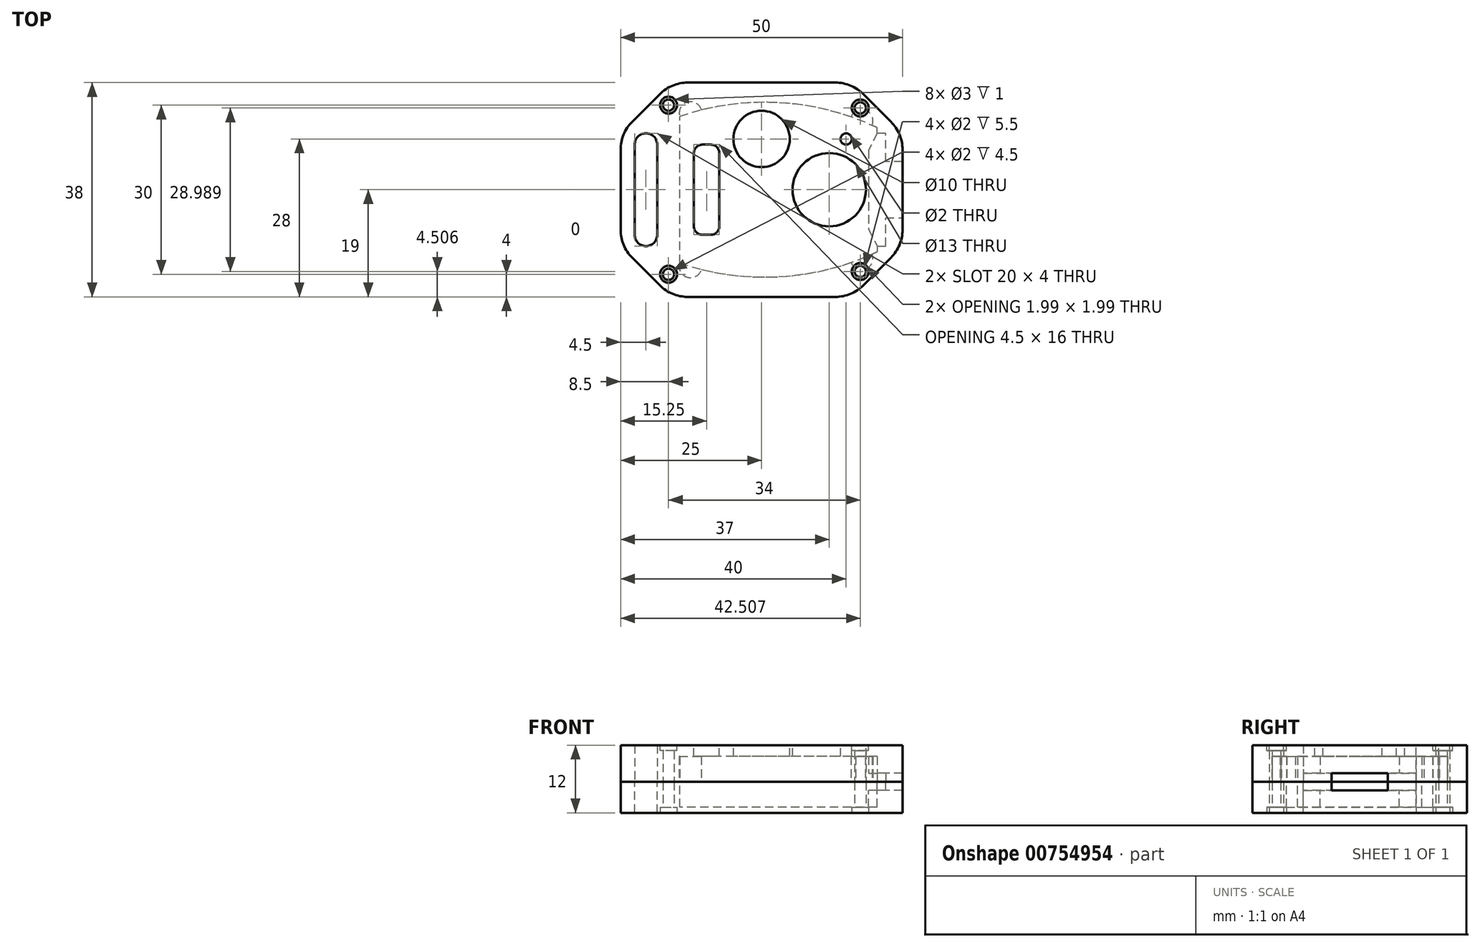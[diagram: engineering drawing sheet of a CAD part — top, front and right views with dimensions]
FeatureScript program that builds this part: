
annotation { "Feature Type Name" : "Feature", "Feature Type Description" : "" }
export const myFeature = defineFeature(function(context is Context, id is Id, definition is map)
    precondition{}
    {
        {
            var Q0;
            Q0=qCreatedBy(makeId("Top.planeOp"),FACE);
            var sketch = newSketch(context, id + "F0", { "sketchPlane" : qUnion([Q0])});
            skLineSegment(sketch, "E0.bottom", {"start": v(25, 19) * mm, "end": v(-25, 19) * mm});
            skLineSegment(sketch, "E0.top", {"start": v(25, -19) * mm, "end": v(-25, -19) * mm});
            skLineSegment(sketch, "E0.left", {"start": v(25, 19) * mm, "end": v(25, -19) * mm});
            skLineSegment(sketch, "E0.right", {"start": v(-25, 19) * mm, "end": v(-25, -19) * mm});
            skPoint(sketch, "E0.middle", {"position": v(0, 0) * mm});
            skLineSegment(sketch, "E1", {"start": v(25, 5) * mm, "end": v(22, 5) * mm});
            skLineSegment(sketch, "E2", {"start": v(22, 5) * mm, "end": v(22, 10) * mm});
            skLineSegment(sketch, "E3", {"start": v(22, 10) * mm, "end": v(20.5, 10) * mm});
            skLineSegment(sketch, "E4", {"start": v(20.5, 10) * mm, "end": v(19, 7) * mm});
            skLineSegment(sketch, "E5", {"start": v(19, 7) * mm, "end": v(19, -7) * mm});
            skLineSegment(sketch, "E6", {"start": v(19, -7) * mm, "end": v(20.5, -10) * mm});
            skLineSegment(sketch, "E7", {"start": v(20.5, -10) * mm, "end": v(22, -10) * mm});
            skLineSegment(sketch, "E8", {"start": v(22, -10) * mm, "end": v(22, -5) * mm});
            skLineSegment(sketch, "E9", {"start": v(22, -5) * mm, "end": v(25, -5) * mm});
            skSolve(sketch);
        }
        {
            var Q0;
            {var subQ1=sQuery(id+"F0.wireOp",EDGE,"E0.bottom");Q0=makeQuery(id+"F0.imprint","IMPRINT",FACE,{"disambiguationData":[TD([[makeQuery(id+"F0.imprint","IMPRINT",EDGE,{"derivedFrom":subQ1}),1.0]])]});}
            var Q1;
            {var subQ0=sQuery(id+"F0.wireOp",EDGE,"E1");Q1=makeQuery(id+"F0.imprint","IMPRINT",FACE,{"disambiguationData":[TD([[makeQuery(id+"F0.imprint","IMPRINT",EDGE,{"derivedFrom":subQ0}),1.0]])]});}
            extrude(context, id + "F1", {"entities" : qUnion([Q0, Q1]), "oppositeDirection" : true, "depth" : 5.5 * mm, "offsetDistance" : 25 * mm});
        }
        {
            var Q0;
            {var subQ0=sQuery(id+"F0.wireOp",EDGE,"E1");Q0=makeQuery(id+"F0.imprint","IMPRINT",FACE,{"disambiguationData":[TD([[makeQuery(id+"F0.imprint","IMPRINT",EDGE,{"derivedFrom":subQ0}),1.0]])]});}
            extrude(context, id + "F2", {"entities" : qUnion([Q0]), "operationType" : NewBodyOperationType.REMOVE, "oppositeDirection" : true, "depth" : 1.5 * mm, "offsetDistance" : 25 * mm});
        }
        {
            var Q0;
            {var subQ1=sQuery(id+"F0.wireOp",EDGE,"E0.bottom");Q0=makeQuery(id+"F0.imprint","IMPRINT",FACE,{"disambiguationData":[TD([[makeQuery(id+"F0.imprint","IMPRINT",EDGE,{"derivedFrom":subQ1}),1.0]])]});}
            var sketch = newSketch(context, id + "F3", { "sketchPlane" : qUnion([Q0])});
            skLineSegment(sketch, "E10.0", {"start": v(20.5, 10) * mm, "end": v(19, 7) * mm});
            skLineSegment(sketch, "E11.0", {"start": v(19, 7) * mm, "end": v(19, -7) * mm});
            skLineSegment(sketch, "E12.0", {"start": v(19, -7) * mm, "end": v(20.5, -10) * mm});
            skLineSegment(sketch, "E13", {"start": v(-14.5, 0) * mm, "end": v(-14.5, 13) * mm});
            skLineSegment(sketch, "E14", {"start": v(-14.5, 0) * mm, "end": v(-14.5, -13) * mm});
            skPoint(sketch, "E15.end.orphan", {"position": v(0.5, 15.5) * mm});
            skPoint(sketch, "E16.end.orphan", {"position": v(0.5, -15.5) * mm});
            skPoint(sketch, "E16.start.orphan", {"position": v(-4.79, 0) * mm});
            skLineSegment(sketch, "E17", {"start": v(20.5, 10) * mm, "end": v(20.5, 11) * mm});
            skLineSegment(sketch, "E18", {"start": v(20.5, -10) * mm, "end": v(20.5, -11) * mm});
            skArc(sketch, "E19", {"start": v(20.5, 11) * mm, "mid": v(3.2, 15.42) * mm, "end": v(-14.5, 13) * mm});
            skArc(sketch, "E20", {"start": v(-14.5, -13) * mm, "mid": v(3.2, -15.42) * mm, "end": v(20.5, -11) * mm});
            skSolve(sketch);
        }
        {
            var Q0;
            Q0=makeQuery(id+"F3.imprint","IMPRINT",FACE,{"disambiguationData":[TD([[makeQuery(id+"F3.imprint","IMPRINT",EDGE,{"derivedFrom":sQuery(id+"F3.wireOp",EDGE,"E10.0")}),-1.0]])]});
            extrude(context, id + "F4", {"entities" : qUnion([Q0]), "operationType" : NewBodyOperationType.REMOVE, "oppositeDirection" : true, "depth" : 4.5 * mm, "offsetDistance" : 25 * mm});
        }
        {
            var Q0;
            Q0=makeQuery(id+"F1.opExtrude","CAP_FACE",FACE,{"disambiguationData":[OSD([sQuery(id+"F0.wireOp",EDGE,"E0.bottom"),sQuery(id+"F0.wireOp",EDGE,"E0.top"),sQuery(id+"F0.wireOp",EDGE,"E0.left"),sQuery(id+"F0.wireOp",EDGE,"E0.right")])],"isStart":true});
            var sketch = newSketch(context, id + "F5", { "sketchPlane" : qUnion([Q0])});
            skLineSegment(sketch, "E21.bottom", {"start": v(-18.5, 10) * mm, "end": v(-22.5, 10) * mm});
            skLineSegment(sketch, "E21.top", {"start": v(-18.5, -10) * mm, "end": v(-22.5, -10) * mm});
            skLineSegment(sketch, "E21.left", {"start": v(-18.5, 10) * mm, "end": v(-18.5, -10) * mm});
            skLineSegment(sketch, "E21.right", {"start": v(-22.5, 10) * mm, "end": v(-22.5, -10) * mm});
            skPoint(sketch, "E21.middle", {"position": v(-20.5, 0) * mm});
            skSolve(sketch);
        }
        {
            var Q0;
            Q0=makeQuery(id+"F5.imprint","IMPRINT",FACE,{"disambiguationData":[TD([[makeQuery(id+"F5.imprint","IMPRINT",EDGE,{"derivedFrom":sQuery(id+"F5.wireOp",EDGE,"E21.bottom")}),1.0]])]});
            extrude(context, id + "F6", {"entities" : qUnion([Q0]), "operationType" : NewBodyOperationType.REMOVE, "oppositeDirection" : true, "depth" : 25 * mm, "offsetDistance" : 25 * mm});
        }
        {
            var Q0;
            {var subQ1=sQuery(id+"F0.wireOp",EDGE,"E0.bottom");Q0=makeQuery(id+"F0.imprint","IMPRINT",FACE,{"disambiguationData":[TD([[makeQuery(id+"F0.imprint","IMPRINT",EDGE,{"derivedFrom":subQ1}),1.0]])]});}
            var Q1;
            {var subQ0=sQuery(id+"F0.wireOp",EDGE,"E1");Q1=makeQuery(id+"F0.imprint","IMPRINT",FACE,{"disambiguationData":[TD([[makeQuery(id+"F0.imprint","IMPRINT",EDGE,{"derivedFrom":subQ0}),1.0]])]});}
            extrude(context, id + "F7", {"entities" : qUnion([Q0, Q1]), "depth" : 6.5 * mm, "offsetDistance" : 25 * mm});
        }
        {
            var Q0;
            {var subQ0=sQuery(id+"F0.wireOp",EDGE,"E1");Q0=makeQuery(id+"F0.imprint","IMPRINT",FACE,{"disambiguationData":[TD([[makeQuery(id+"F0.imprint","IMPRINT",EDGE,{"derivedFrom":subQ0}),1.0]])]});}
            extrude(context, id + "F8", {"entities" : qUnion([Q0]), "operationType" : NewBodyOperationType.REMOVE, "depth" : 1.5 * mm, "offsetDistance" : 25 * mm});
        }
        {
            var Q0;
            Q0=makeQuery(id+"F3.imprint","IMPRINT",FACE,{"disambiguationData":[TD([[makeQuery(id+"F3.imprint","IMPRINT",EDGE,{"derivedFrom":sQuery(id+"F3.wireOp",EDGE,"E10.0")}),-1.0]])]});
            extrude(context, id + "F9", {"entities" : qUnion([Q0]), "operationType" : NewBodyOperationType.REMOVE, "depth" : 4.5 * mm, "offsetDistance" : 25 * mm});
        }
        {
            var Q0;
            Q0=makeQuery(id+"F5.imprint","IMPRINT",FACE,{"disambiguationData":[TD([[makeQuery(id+"F5.imprint","IMPRINT",EDGE,{"derivedFrom":sQuery(id+"F5.wireOp",EDGE,"E21.bottom")}),1.0]])]});
            extrude(context, id + "F10", {"entities" : qUnion([Q0]), "operationType" : NewBodyOperationType.REMOVE, "depth" : 25 * mm, "offsetDistance" : 25 * mm});
        }
        {
            var Q0;
            Q0=makeQuery(id+"F7.opExtrude","CAP_FACE",FACE,{"disambiguationData":[OSD([sQuery(id+"F0.wireOp",EDGE,"E0.bottom"),sQuery(id+"F0.wireOp",EDGE,"E0.top"),sQuery(id+"F0.wireOp",EDGE,"E0.left"),sQuery(id+"F0.wireOp",EDGE,"E0.right")])],"isStart":false});
            var sketch = newSketch(context, id + "F11", { "sketchPlane" : qUnion([Q0])});
            skCircle(sketch, "E22", {"center": v(12, 0) * mm, "radius": 6.5 * mm});
            skCircle(sketch, "E23", {"center": v(0, 9) * mm, "radius": 5 * mm});
            skLineSegment(sketch, "E24.bottom", {"start": v(-9, 8) * mm, "end": v(-10.5, 8) * mm});
            skLineSegment(sketch, "E24.top", {"start": v(-9, -8) * mm, "end": v(-10.5, -8) * mm});
            skLineSegment(sketch, "E24.left", {"start": v(-7.5, 6.5) * mm, "end": v(-7.5, -6.5) * mm});
            skLineSegment(sketch, "E24.right", {"start": v(-12, 6.5) * mm, "end": v(-12, -6.5) * mm});
            skPoint(sketch, "E24.middle", {"position": v(-9.75, 0) * mm});
            skPoint(sketch, "E25.visualSharp", {"position": v(-12, 8) * mm});
            skArc(sketch, "E25.filletArc", {"start": v(-10.5, 8) * mm, "mid": v(-11.56, 7.56) * mm, "end": v(-12, 6.5) * mm});
            skPoint(sketch, "E26.visualSharp", {"position": v(-7.5, 8) * mm});
            skArc(sketch, "E26.filletArc", {"start": v(-7.5, 6.5) * mm, "mid": v(-7.94, 7.56) * mm, "end": v(-9, 8) * mm});
            skPoint(sketch, "E27.visualSharp", {"position": v(-7.5, -8) * mm});
            skArc(sketch, "E27.filletArc", {"start": v(-9, -8) * mm, "mid": v(-7.94, -7.56) * mm, "end": v(-7.5, -6.5) * mm});
            skPoint(sketch, "E28.visualSharp", {"position": v(-12, -8) * mm});
            skArc(sketch, "E28.filletArc", {"start": v(-12, -6.5) * mm, "mid": v(-11.56, -7.56) * mm, "end": v(-10.5, -8) * mm});
            skCircle(sketch, "E29", {"center": v(15, 9) * mm, "radius": 1 * mm});
            skSolve(sketch);
        }
        {
            var Q0;
            Q0=makeQuery(id+"F11.imprint","IMPRINT",FACE,{"disambiguationData":[TD([[makeQuery(id+"F11.imprint","IMPRINT",EDGE,{"derivedFrom":sQuery(id+"F11.wireOp",EDGE,"E23")}),1.0]])]});
            var Q1;
            Q1=makeQuery(id+"F11.imprint","IMPRINT",FACE,{"disambiguationData":[TD([[makeQuery(id+"F11.imprint","IMPRINT",EDGE,{"derivedFrom":sQuery(id+"F11.wireOp",EDGE,"E24.bottom")}),1.0]])]});
            var Q2;
            Q2=makeQuery(id+"F11.imprint","IMPRINT",FACE,{"disambiguationData":[TD([[makeQuery(id+"F11.imprint","IMPRINT",EDGE,{"derivedFrom":sQuery(id+"F11.wireOp",EDGE,"E22")}),1.0]])]});
            var Q3;
            Q3=makeQuery(id+"F11.imprint","IMPRINT",FACE,{"disambiguationData":[TD([[makeQuery(id+"F11.imprint","IMPRINT",EDGE,{"derivedFrom":sQuery(id+"F11.wireOp",EDGE,"E29")}),1.0]])]});
            extrude(context, id + "F12", {"entities" : qUnion([Q0, Q1, Q2, Q3]), "operationType" : NewBodyOperationType.REMOVE, "oppositeDirection" : true, "depth" : 4 * mm, "offsetDistance" : 25 * mm});
        }
        {
            var Q0;
            Q0=makeQuery(id+"F3.imprint","IMPRINT",FACE,{"disambiguationData":[TD([[makeQuery(id+"F3.imprint","IMPRINT",EDGE,{"derivedFrom":sQuery(id+"F3.wireOp",EDGE,"E13")}),1.0]])]});
            var sketch = newSketch(context, id + "F13", { "sketchPlane" : qUnion([Q0])});
            skArc(sketch, "E30.0", {"start": v(-14.5, -13) * mm, "mid": v(3.2, -15.42) * mm, "end": v(20.5, -11) * mm});
            skArc(sketch, "E31.0", {"start": v(20.5, 11) * mm, "mid": v(3.2, 15.42) * mm, "end": v(-14.5, 13) * mm});
            skArc(sketch, "E32", {"start": v(-14.5, -13) * mm, "mid": v(-13.16, -15.52) * mm, "end": v(-10.66, -14.13) * mm});
            skArc(sketch, "E33", {"start": v(15.88, -12.9) * mm, "mid": v(18.5, -14.06) * mm, "end": v(19.6, -11.42) * mm});
            skArc(sketch, "E34", {"start": v(-10.66, 14.13) * mm, "mid": v(-13.16, 15.52) * mm, "end": v(-14.5, 13) * mm});
            skArc(sketch, "E35", {"start": v(19.6, 11.42) * mm, "mid": v(18.5, 14.06) * mm, "end": v(15.88, 12.9) * mm});
            skLineSegment(sketch, "E36", {"start": v(-14.5, -13) * mm, "end": v(-10.66, -14.13) * mm});
            skLineSegment(sketch, "E37", {"start": v(15.88, -12.9) * mm, "end": v(19.6, -11.42) * mm});
            skLineSegment(sketch, "E38", {"start": v(19.6, 11.42) * mm, "end": v(15.88, 12.9) * mm});
            skLineSegment(sketch, "E39", {"start": v(-10.66, 14.13) * mm, "end": v(-14.5, 13) * mm});
            skSolve(sketch);
        }
        {
            var Q0;
            Q0 = qSketchRegion(id + "F13", true);
            extrude(context, id + "F14", {"entities" : qUnion([Q0]), "operationType" : NewBodyOperationType.REMOVE, "depth" : 4.5 * mm, "offsetDistance" : 25 * mm});
        }
        {
            var Q0;
            Q0=makeQuery(id+"F7.opExtrude","SWEPT_EDGE",EDGE,{"disambiguationData":[OSD([sQuery(id+"F0.wireOp",EDGE,"E0.top"),sQuery(id+"F0.wireOp",EDGE,"E0.left")])]});
            var Q1;
            Q1=makeQuery(id+"F1.opExtrude","SWEPT_EDGE",EDGE,{"disambiguationData":[OSD([sQuery(id+"F0.wireOp",EDGE,"E0.top"),sQuery(id+"F0.wireOp",EDGE,"E0.left")])]});
            var Q2;
            Q2=makeQuery(id+"F1.opExtrude","SWEPT_EDGE",EDGE,{"disambiguationData":[OSD([sQuery(id+"F0.wireOp",EDGE,"E0.bottom"),sQuery(id+"F0.wireOp",EDGE,"E0.left")])]});
            var Q3;
            Q3=makeQuery(id+"F7.opExtrude","SWEPT_EDGE",EDGE,{"disambiguationData":[OSD([sQuery(id+"F0.wireOp",EDGE,"E0.bottom"),sQuery(id+"F0.wireOp",EDGE,"E0.left")])]});
            var Q4;
            Q4=makeQuery(id+"F7.opExtrude","SWEPT_EDGE",EDGE,{"disambiguationData":[OSD([sQuery(id+"F0.wireOp",EDGE,"E0.top"),sQuery(id+"F0.wireOp",EDGE,"E0.right")])]});
            var Q5;
            Q5=makeQuery(id+"F1.opExtrude","SWEPT_EDGE",EDGE,{"disambiguationData":[OSD([sQuery(id+"F0.wireOp",EDGE,"E0.top"),sQuery(id+"F0.wireOp",EDGE,"E0.right")])]});
            var Q6;
            Q6=makeQuery(id+"F7.opExtrude","SWEPT_EDGE",EDGE,{"disambiguationData":[OSD([sQuery(id+"F0.wireOp",EDGE,"E0.bottom"),sQuery(id+"F0.wireOp",EDGE,"E0.right")])]});
            var Q7;
            Q7=makeQuery(id+"F1.opExtrude","SWEPT_EDGE",EDGE,{"disambiguationData":[OSD([sQuery(id+"F0.wireOp",EDGE,"E0.bottom"),sQuery(id+"F0.wireOp",EDGE,"E0.right")])]});
            chamfer(context, id + "F15", {"entities" : qUnion([Q0, Q1, Q2, Q3, Q4, Q5, Q6, Q7]), "width" : 9 * mm, "tangentPropagation" : true});
        }
        {
            var Q0;
            {var subQ0=sQuery(id+"F0.wireOp",EDGE,"E0.top");Q0=makeQuery(id+"F15.opChamfer","BLEND_EDGE",EDGE,{"blendedFrom":[makeQuery(id+"F7.opExtrude","SWEPT_EDGE",EDGE,{"disambiguationData":[OSD([subQ0,sQuery(id+"F0.wireOp",EDGE,"E0.left")])]}),makeQuery(id+"F7.opExtrude","SWEPT_FACE",FACE,{"disambiguationData":[OSD([subQ0])]})],"blendedInto":[makeQuery(id+"F7.opExtrude","SWEPT_FACE",FACE,{"disambiguationData":[OSD([subQ0])]})]});}
            var Q1;
            {var subQ0=sQuery(id+"F0.wireOp",EDGE,"E0.top");Q1=makeQuery(id+"F15.opChamfer","BLEND_EDGE",EDGE,{"blendedFrom":[makeQuery(id+"F1.opExtrude","SWEPT_EDGE",EDGE,{"disambiguationData":[OSD([subQ0,sQuery(id+"F0.wireOp",EDGE,"E0.left")])]}),makeQuery(id+"F1.opExtrude","SWEPT_FACE",FACE,{"disambiguationData":[OSD([subQ0])]})],"blendedInto":[makeQuery(id+"F1.opExtrude","SWEPT_FACE",FACE,{"disambiguationData":[OSD([subQ0])]})]});}
            var Q2;
            {var subQ0=sQuery(id+"F0.wireOp",EDGE,"E0.left");Q2=makeQuery(id+"F15.opChamfer","BLEND_EDGE",EDGE,{"blendedFrom":[makeQuery(id+"F1.opExtrude","SWEPT_EDGE",EDGE,{"disambiguationData":[OSD([sQuery(id+"F0.wireOp",EDGE,"E0.top"),subQ0])]}),makeQuery(id+"F1.opExtrude","SWEPT_FACE",FACE,{"disambiguationData":[OSD([subQ0])]})],"blendedInto":[makeQuery(id+"F1.opExtrude","SWEPT_FACE",FACE,{"disambiguationData":[OSD([subQ0])]})]});}
            var Q3;
            {var subQ0=sQuery(id+"F0.wireOp",EDGE,"E0.left");Q3=makeQuery(id+"F15.opChamfer","BLEND_EDGE",EDGE,{"blendedFrom":[makeQuery(id+"F7.opExtrude","SWEPT_EDGE",EDGE,{"disambiguationData":[OSD([sQuery(id+"F0.wireOp",EDGE,"E0.top"),subQ0])]}),makeQuery(id+"F7.opExtrude","SWEPT_FACE",FACE,{"disambiguationData":[OSD([subQ0])]})],"blendedInto":[makeQuery(id+"F7.opExtrude","SWEPT_FACE",FACE,{"disambiguationData":[OSD([subQ0])]})]});}
            var Q4;
            {var subQ0=sQuery(id+"F0.wireOp",EDGE,"E0.left");Q4=makeQuery(id+"F15.opChamfer","BLEND_EDGE",EDGE,{"blendedFrom":[makeQuery(id+"F1.opExtrude","SWEPT_EDGE",EDGE,{"disambiguationData":[OSD([sQuery(id+"F0.wireOp",EDGE,"E0.bottom"),subQ0])]}),makeQuery(id+"F1.opExtrude","SWEPT_FACE",FACE,{"disambiguationData":[OSD([subQ0])]})],"blendedInto":[makeQuery(id+"F1.opExtrude","SWEPT_FACE",FACE,{"disambiguationData":[OSD([subQ0])]})]});}
            var Q5;
            {var subQ0=sQuery(id+"F0.wireOp",EDGE,"E0.left");Q5=makeQuery(id+"F15.opChamfer","BLEND_EDGE",EDGE,{"blendedFrom":[makeQuery(id+"F7.opExtrude","SWEPT_EDGE",EDGE,{"disambiguationData":[OSD([sQuery(id+"F0.wireOp",EDGE,"E0.bottom"),subQ0])]}),makeQuery(id+"F7.opExtrude","SWEPT_FACE",FACE,{"disambiguationData":[OSD([subQ0])]})],"blendedInto":[makeQuery(id+"F7.opExtrude","SWEPT_FACE",FACE,{"disambiguationData":[OSD([subQ0])]})]});}
            var Q6;
            {var subQ0=sQuery(id+"F0.wireOp",EDGE,"E0.bottom");Q6=makeQuery(id+"F15.opChamfer","BLEND_EDGE",EDGE,{"blendedFrom":[makeQuery(id+"F7.opExtrude","SWEPT_EDGE",EDGE,{"disambiguationData":[OSD([subQ0,sQuery(id+"F0.wireOp",EDGE,"E0.left")])]}),makeQuery(id+"F7.opExtrude","SWEPT_FACE",FACE,{"disambiguationData":[OSD([subQ0])]})],"blendedInto":[makeQuery(id+"F7.opExtrude","SWEPT_FACE",FACE,{"disambiguationData":[OSD([subQ0])]})]});}
            var Q7;
            {var subQ0=sQuery(id+"F0.wireOp",EDGE,"E0.bottom");Q7=makeQuery(id+"F15.opChamfer","BLEND_EDGE",EDGE,{"blendedFrom":[makeQuery(id+"F1.opExtrude","SWEPT_EDGE",EDGE,{"disambiguationData":[OSD([subQ0,sQuery(id+"F0.wireOp",EDGE,"E0.left")])]}),makeQuery(id+"F1.opExtrude","SWEPT_FACE",FACE,{"disambiguationData":[OSD([subQ0])]})],"blendedInto":[makeQuery(id+"F1.opExtrude","SWEPT_FACE",FACE,{"disambiguationData":[OSD([subQ0])]})]});}
            var Q8;
            {var subQ0=sQuery(id+"F0.wireOp",EDGE,"E0.top");Q8=makeQuery(id+"F15.opChamfer","BLEND_EDGE",EDGE,{"blendedFrom":[makeQuery(id+"F1.opExtrude","SWEPT_EDGE",EDGE,{"disambiguationData":[OSD([subQ0,sQuery(id+"F0.wireOp",EDGE,"E0.right")])]}),makeQuery(id+"F1.opExtrude","SWEPT_FACE",FACE,{"disambiguationData":[OSD([subQ0])]})],"blendedInto":[makeQuery(id+"F1.opExtrude","SWEPT_FACE",FACE,{"disambiguationData":[OSD([subQ0])]})]});}
            var Q9;
            {var subQ0=sQuery(id+"F0.wireOp",EDGE,"E0.top");Q9=makeQuery(id+"F15.opChamfer","BLEND_EDGE",EDGE,{"blendedFrom":[makeQuery(id+"F7.opExtrude","SWEPT_EDGE",EDGE,{"disambiguationData":[OSD([subQ0,sQuery(id+"F0.wireOp",EDGE,"E0.right")])]}),makeQuery(id+"F7.opExtrude","SWEPT_FACE",FACE,{"disambiguationData":[OSD([subQ0])]})],"blendedInto":[makeQuery(id+"F7.opExtrude","SWEPT_FACE",FACE,{"disambiguationData":[OSD([subQ0])]})]});}
            var Q10;
            {var subQ0=sQuery(id+"F0.wireOp",EDGE,"E0.right");Q10=makeQuery(id+"F15.opChamfer","BLEND_EDGE",EDGE,{"blendedFrom":[makeQuery(id+"F7.opExtrude","SWEPT_EDGE",EDGE,{"disambiguationData":[OSD([sQuery(id+"F0.wireOp",EDGE,"E0.top"),subQ0])]}),makeQuery(id+"F7.opExtrude","SWEPT_FACE",FACE,{"disambiguationData":[OSD([subQ0])]})],"blendedInto":[makeQuery(id+"F7.opExtrude","SWEPT_FACE",FACE,{"disambiguationData":[OSD([subQ0])]})]});}
            var Q11;
            {var subQ0=sQuery(id+"F0.wireOp",EDGE,"E0.right");Q11=makeQuery(id+"F15.opChamfer","BLEND_EDGE",EDGE,{"blendedFrom":[makeQuery(id+"F1.opExtrude","SWEPT_EDGE",EDGE,{"disambiguationData":[OSD([sQuery(id+"F0.wireOp",EDGE,"E0.top"),subQ0])]}),makeQuery(id+"F1.opExtrude","SWEPT_FACE",FACE,{"disambiguationData":[OSD([subQ0])]})],"blendedInto":[makeQuery(id+"F1.opExtrude","SWEPT_FACE",FACE,{"disambiguationData":[OSD([subQ0])]})]});}
            var Q12;
            {var subQ0=sQuery(id+"F0.wireOp",EDGE,"E0.right");Q12=makeQuery(id+"F15.opChamfer","BLEND_EDGE",EDGE,{"blendedFrom":[makeQuery(id+"F1.opExtrude","SWEPT_EDGE",EDGE,{"disambiguationData":[OSD([sQuery(id+"F0.wireOp",EDGE,"E0.bottom"),subQ0])]}),makeQuery(id+"F1.opExtrude","SWEPT_FACE",FACE,{"disambiguationData":[OSD([subQ0])]})],"blendedInto":[makeQuery(id+"F1.opExtrude","SWEPT_FACE",FACE,{"disambiguationData":[OSD([subQ0])]})]});}
            var Q13;
            {var subQ0=sQuery(id+"F0.wireOp",EDGE,"E0.right");Q13=makeQuery(id+"F15.opChamfer","BLEND_EDGE",EDGE,{"blendedFrom":[makeQuery(id+"F7.opExtrude","SWEPT_EDGE",EDGE,{"disambiguationData":[OSD([sQuery(id+"F0.wireOp",EDGE,"E0.bottom"),subQ0])]}),makeQuery(id+"F7.opExtrude","SWEPT_FACE",FACE,{"disambiguationData":[OSD([subQ0])]})],"blendedInto":[makeQuery(id+"F7.opExtrude","SWEPT_FACE",FACE,{"disambiguationData":[OSD([subQ0])]})]});}
            var Q14;
            {var subQ0=sQuery(id+"F0.wireOp",EDGE,"E0.bottom");Q14=makeQuery(id+"F15.opChamfer","BLEND_EDGE",EDGE,{"blendedFrom":[makeQuery(id+"F1.opExtrude","SWEPT_EDGE",EDGE,{"disambiguationData":[OSD([subQ0,sQuery(id+"F0.wireOp",EDGE,"E0.right")])]}),makeQuery(id+"F1.opExtrude","SWEPT_FACE",FACE,{"disambiguationData":[OSD([subQ0])]})],"blendedInto":[makeQuery(id+"F1.opExtrude","SWEPT_FACE",FACE,{"disambiguationData":[OSD([subQ0])]})]});}
            var Q15;
            {var subQ0=sQuery(id+"F0.wireOp",EDGE,"E0.bottom");Q15=makeQuery(id+"F15.opChamfer","BLEND_EDGE",EDGE,{"blendedFrom":[makeQuery(id+"F7.opExtrude","SWEPT_EDGE",EDGE,{"disambiguationData":[OSD([subQ0,sQuery(id+"F0.wireOp",EDGE,"E0.right")])]}),makeQuery(id+"F7.opExtrude","SWEPT_FACE",FACE,{"disambiguationData":[OSD([subQ0])]})],"blendedInto":[makeQuery(id+"F7.opExtrude","SWEPT_FACE",FACE,{"disambiguationData":[OSD([subQ0])]})]});}
            fillet(context, id + "F16", {"entities" : qUnion([Q0, Q1, Q2, Q3, Q4, Q5, Q6, Q7, Q8, Q9, Q10, Q11, Q12, Q13, Q14, Q15]), "radius" : 7 * mm, "tangentPropagation" : true, "allowEdgeOverflow" : false});
        }
        {
            var Q0;
            Q0=makeQuery(id+"F6.boolean.opBoolean","COPY",EDGE,{"derivedFrom":makeQuery(id+"F6.opExtrude","SWEPT_EDGE",EDGE,{"disambiguationData":[OSD([sQuery(id+"F5.wireOp",EDGE,"E21.bottom"),sQuery(id+"F5.wireOp",EDGE,"E21.right")])]})});
            var Q1;
            Q1=makeQuery(id+"F10.boolean.opBoolean","COPY",EDGE,{"derivedFrom":makeQuery(id+"F10.opExtrude","SWEPT_EDGE",EDGE,{"disambiguationData":[OSD([sQuery(id+"F5.wireOp",EDGE,"E21.bottom"),sQuery(id+"F5.wireOp",EDGE,"E21.right")])]})});
            var Q2;
            Q2=makeQuery(id+"F10.boolean.opBoolean","COPY",EDGE,{"derivedFrom":makeQuery(id+"F10.opExtrude","SWEPT_EDGE",EDGE,{"disambiguationData":[OSD([sQuery(id+"F5.wireOp",EDGE,"E21.top"),sQuery(id+"F5.wireOp",EDGE,"E21.right")])]})});
            var Q3;
            Q3=makeQuery(id+"F6.boolean.opBoolean","COPY",EDGE,{"derivedFrom":makeQuery(id+"F6.opExtrude","SWEPT_EDGE",EDGE,{"disambiguationData":[OSD([sQuery(id+"F5.wireOp",EDGE,"E21.top"),sQuery(id+"F5.wireOp",EDGE,"E21.right")])]})});
            var Q4;
            Q4=makeQuery(id+"F6.boolean.opBoolean","COPY",EDGE,{"derivedFrom":makeQuery(id+"F6.opExtrude","SWEPT_EDGE",EDGE,{"disambiguationData":[OSD([sQuery(id+"F5.wireOp",EDGE,"E21.bottom"),sQuery(id+"F5.wireOp",EDGE,"E21.left")])]})});
            var Q5;
            Q5=makeQuery(id+"F10.boolean.opBoolean","COPY",EDGE,{"derivedFrom":makeQuery(id+"F10.opExtrude","SWEPT_EDGE",EDGE,{"disambiguationData":[OSD([sQuery(id+"F5.wireOp",EDGE,"E21.bottom"),sQuery(id+"F5.wireOp",EDGE,"E21.left")])]})});
            var Q6;
            Q6=makeQuery(id+"F10.boolean.opBoolean","COPY",EDGE,{"derivedFrom":makeQuery(id+"F10.opExtrude","SWEPT_EDGE",EDGE,{"disambiguationData":[OSD([sQuery(id+"F5.wireOp",EDGE,"E21.top"),sQuery(id+"F5.wireOp",EDGE,"E21.left")])]})});
            var Q7;
            Q7=makeQuery(id+"F6.boolean.opBoolean","COPY",EDGE,{"derivedFrom":makeQuery(id+"F6.opExtrude","SWEPT_EDGE",EDGE,{"disambiguationData":[OSD([sQuery(id+"F5.wireOp",EDGE,"E21.top"),sQuery(id+"F5.wireOp",EDGE,"E21.left")])]})});
            fillet(context, id + "F17", {"entities" : qUnion([Q0, Q1, Q2, Q3, Q4, Q5, Q6, Q7]), "radius" : 2 * mm, "tangentPropagation" : true, "allowEdgeOverflow" : false});
        }
        {
            var Q0;
            {var subQ1=sQuery(id+"F0.wireOp",EDGE,"E0.bottom");Q0=makeQuery(id+"F0.imprint","IMPRINT",FACE,{"disambiguationData":[TD([[makeQuery(id+"F0.imprint","IMPRINT",EDGE,{"derivedFrom":subQ1}),1.0]])]});}
            var sketch = newSketch(context, id + "F18", { "sketchPlane" : qUnion([Q0])});
            skCircle(sketch, "E40", {"center": v(17.5, 14.5) * mm, "radius": 1 * mm});
            skCircle(sketch, "E41", {"center": v(-16.5, 15) * mm, "radius": 1 * mm});
            skCircle(sketch, "E42", {"center": v(-16.5, -15) * mm, "radius": 1 * mm});
            skCircle(sketch, "E43", {"center": v(17.5, -14.5) * mm, "radius": 1 * mm});
            skSolve(sketch);
        }
        {
            var Q0;
            Q0=makeQuery(id+"F18.imprint","IMPRINT",FACE,{"disambiguationData":[TD([[makeQuery(id+"F18.imprint","IMPRINT",EDGE,{"derivedFrom":sQuery(id+"F18.wireOp",EDGE,"E40")}),1.0]])]});
            var Q1;
            Q1=makeQuery(id+"F18.imprint","IMPRINT",FACE,{"disambiguationData":[TD([[makeQuery(id+"F18.imprint","IMPRINT",EDGE,{"derivedFrom":sQuery(id+"F18.wireOp",EDGE,"E41")}),1.0]])]});
            var Q2;
            Q2=makeQuery(id+"F18.imprint","IMPRINT",FACE,{"disambiguationData":[TD([[makeQuery(id+"F18.imprint","IMPRINT",EDGE,{"derivedFrom":sQuery(id+"F18.wireOp",EDGE,"E42")}),1.0]])]});
            var Q3;
            Q3=makeQuery(id+"F18.imprint","IMPRINT",FACE,{"disambiguationData":[TD([[makeQuery(id+"F18.imprint","IMPRINT",EDGE,{"derivedFrom":sQuery(id+"F18.wireOp",EDGE,"E43")}),1.0]])]});
            extrude(context, id + "F19", {"entities" : qUnion([Q0, Q1, Q2, Q3]), "operationType" : NewBodyOperationType.REMOVE, "endBound" : BoundingType.SYMMETRIC, "depth" : 15 * mm, "offsetDistance" : 25 * mm});
        }
        {
            var Q0;
            Q0=makeQuery(id+"F7.opExtrude","CAP_FACE",FACE,{"disambiguationData":[OSD([sQuery(id+"F0.wireOp",EDGE,"E0.bottom"),sQuery(id+"F0.wireOp",EDGE,"E0.top"),sQuery(id+"F0.wireOp",EDGE,"E0.left"),sQuery(id+"F0.wireOp",EDGE,"E0.right")])],"isStart":false});
            var sketch = newSketch(context, id + "F20", { "sketchPlane" : qUnion([Q0])});
            skCircle(sketch, "E44", {"center": v(-16.5, -15) * mm, "radius": 1.5 * mm});
            skCircle(sketch, "E45", {"center": v(-16.5, 15) * mm, "radius": 1.5 * mm});
            skCircle(sketch, "E46", {"center": v(17.5, 14.5) * mm, "radius": 1.5 * mm});
            skCircle(sketch, "E47", {"center": v(17.5, -14.5) * mm, "radius": 1.5 * mm});
            skSolve(sketch);
        }
        {
            var Q0;
            Q0=makeQuery(id+"F20.imprint","IMPRINT",FACE,{"disambiguationData":[TD([[makeQuery(id+"F20.imprint","IMPRINT",EDGE,{"derivedFrom":sQuery(id+"F20.wireOp",EDGE,"E44")}),1.0]])]});
            var Q1;
            Q1=makeQuery(id+"F20.imprint","IMPRINT",FACE,{"disambiguationData":[TD([[makeQuery(id+"F20.imprint","IMPRINT",EDGE,{"derivedFrom":sQuery(id+"F20.wireOp",EDGE,"E45")}),1.0]])]});
            var Q2;
            Q2=makeQuery(id+"F20.imprint","IMPRINT",FACE,{"disambiguationData":[TD([[makeQuery(id+"F20.imprint","IMPRINT",EDGE,{"derivedFrom":sQuery(id+"F20.wireOp",EDGE,"E46")}),1.0]])]});
            var Q3;
            Q3=makeQuery(id+"F20.imprint","IMPRINT",FACE,{"disambiguationData":[TD([[makeQuery(id+"F20.imprint","IMPRINT",EDGE,{"derivedFrom":sQuery(id+"F20.wireOp",EDGE,"E47")}),1.0]])]});
            extrude(context, id + "F21", {"entities" : qUnion([Q0, Q1, Q2, Q3]), "operationType" : NewBodyOperationType.REMOVE, "oppositeDirection" : true, "depth" : 1 * mm, "offsetDistance" : 25 * mm});
        }
        {
            var Q0;
            Q0=makeQuery(id+"F1.opExtrude","CAP_FACE",FACE,{"disambiguationData":[OSD([sQuery(id+"F0.wireOp",EDGE,"E0.bottom"),sQuery(id+"F0.wireOp",EDGE,"E0.top"),sQuery(id+"F0.wireOp",EDGE,"E0.left"),sQuery(id+"F0.wireOp",EDGE,"E0.right")])],"isStart":false});
            var sketch = newSketch(context, id + "F22", { "sketchPlane" : qUnion([Q0])});
            skCircle(sketch, "E48", {"center": v(-16.5, 15) * mm, "radius": 1.5 * mm});
            skCircle(sketch, "E49", {"center": v(17.5, 14.5) * mm, "radius": 1.5 * mm});
            skCircle(sketch, "E50", {"center": v(-16.5, -15) * mm, "radius": 1.5 * mm});
            skCircle(sketch, "E51", {"center": v(17.5, -14.5) * mm, "radius": 1.5 * mm});
            skSolve(sketch);
        }
        {
            var Q0;
            Q0 = qSketchRegion(id + "F22", true);
            extrude(context, id + "F23", {"entities" : qUnion([Q0]), "operationType" : NewBodyOperationType.REMOVE, "oppositeDirection" : true, "depth" : 1 * mm, "offsetDistance" : 25 * mm});
        }
    });
